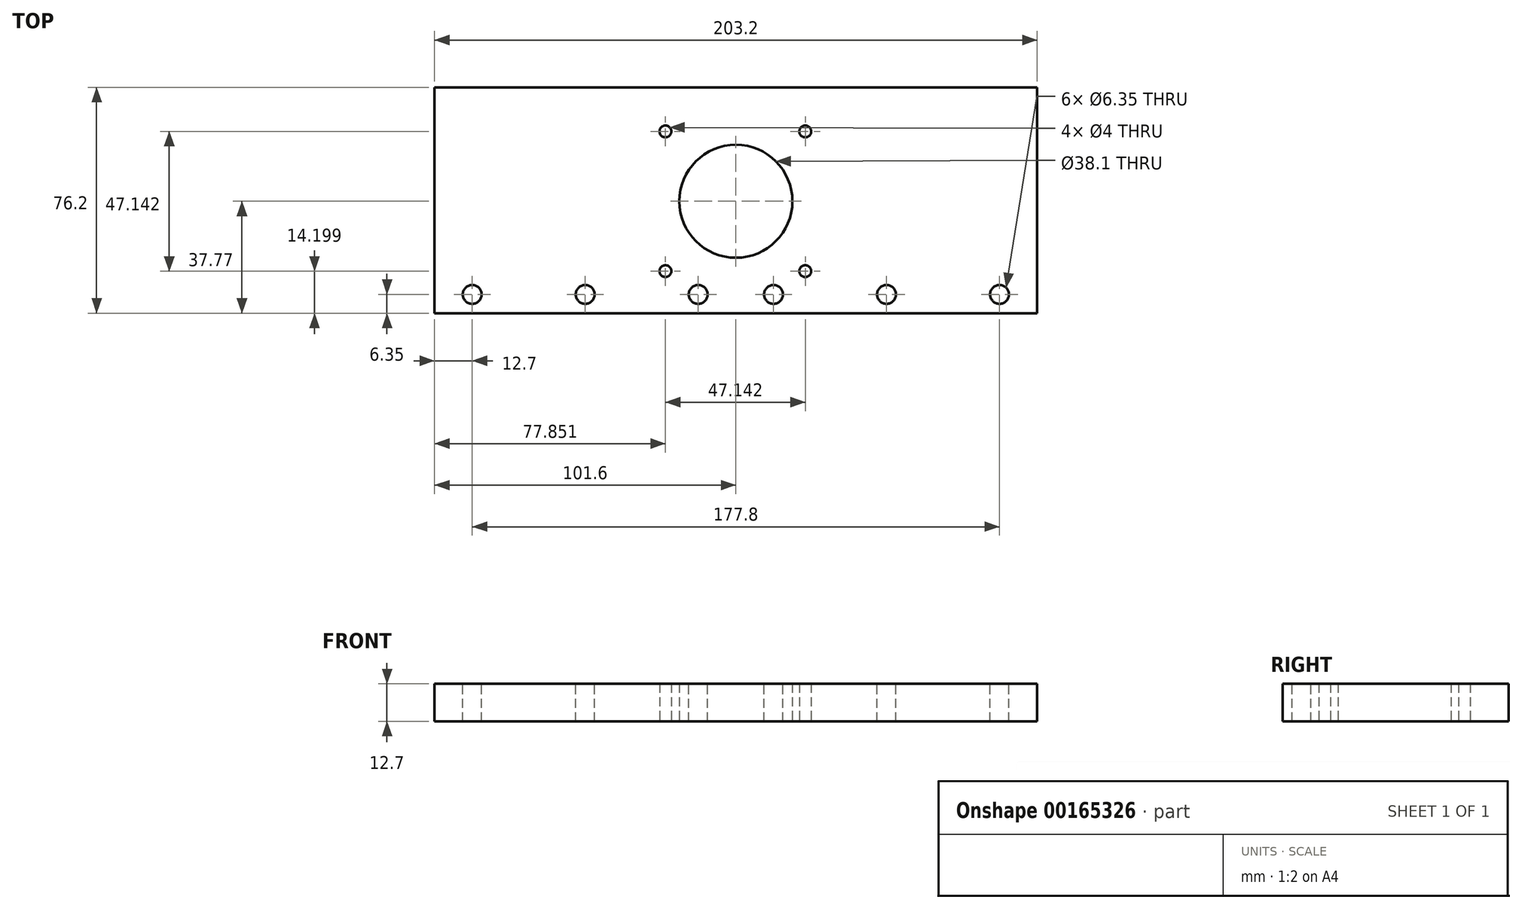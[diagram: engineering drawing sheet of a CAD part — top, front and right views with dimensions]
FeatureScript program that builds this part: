
annotation { "Feature Type Name" : "Feature", "Feature Type Description" : "" }
export const myFeature = defineFeature(function(context is Context, id is Id, definition is map)
    precondition{}
    {
        {
            var Q0;
            Q0=qCreatedBy(makeId("Top.planeOp"),FACE);
            var sketch = newSketch(context, id + "F0", { "sketchPlane" : qUnion([Q0])});
            skLineSegment(sketch, "E0.rect.bottom", {"start": v(101.6, -38.1) * mm, "end": v(-101.6, -38.1) * mm});
            skLineSegment(sketch, "E0.rect.top", {"start": v(101.6, 38.1) * mm, "end": v(-101.6, 38.1) * mm});
            skLineSegment(sketch, "E0.rect.left", {"start": v(101.6, -38.1) * mm, "end": v(101.6, 38.1) * mm});
            skLineSegment(sketch, "E0.rect.right", {"start": v(-101.6, -38.1) * mm, "end": v(-101.6, 38.1) * mm});
            skPoint(sketch, "E0.rect.middle", {"position": v(0, 0) * mm});
            skLineSegment(sketch, "E1", {"start": v(-101.6, 23.24) * mm, "end": v(101.6, 23.24) * mm, "construction": true});
            skLineSegment(sketch, "E2", {"start": v(101.6, 23.24) * mm, "end": v(102.39, 23.56) * mm, "construction": true});
            skLineSegment(sketch, "E3", {"start": v(-23.75, 38.1) * mm, "end": v(-23.75, -38.1) * mm, "construction": true});
            skLineSegment(sketch, "E4", {"start": v(-23.75, -38.1) * mm, "end": v(-24.87, -37.47) * mm, "construction": true});
            skLineSegment(sketch, "E5", {"start": v(-101.6, -23.9) * mm, "end": v(101.6, -23.9) * mm, "construction": true});
            skLineSegment(sketch, "E6", {"start": v(23.4, 38.1) * mm, "end": v(23.4, -38.1) * mm, "construction": true});
            skLineSegment(sketch, "E7", {"start": v(-23.75, 23.24) * mm, "end": v(23.4, -23.9) * mm, "construction": true});
            skLineSegment(sketch, "E8", {"start": v(23.4, 23.24) * mm, "end": v(-23.75, -23.9) * mm, "construction": true});
            skCircle(sketch, "E9", {"center": v(0, -0.33) * mm, "radius": 19.05 * mm});
            skPoint(sketch, "E9.centerSnap0", {"position": v(-0.18, -0.33) * mm});
            skCircle(sketch, "E10", {"center": v(-23.75, 23.24) * mm, "radius": 2 * mm});
            skCircle(sketch, "E11", {"center": v(-23.75, -23.9) * mm, "radius": 2 * mm});
            skCircle(sketch, "E12", {"center": v(23.4, -23.9) * mm, "radius": 2 * mm});
            skCircle(sketch, "E13", {"center": v(23.4, 23.24) * mm, "radius": 2 * mm});
            skSolve(sketch);
        }
        {
            var Q0;
            Q0=qSketchRegion(id+"F0",true);
            extrude(context, id + "F1", {"entities" : qUnion([Q0]), "depth" : 12.7 * mm});
        }
        {
            var Q0;
            Q0=makeQuery(id+"F1.opExtrude","CAP_FACE",FACE,{"disambiguationData":[OSD([sQuery(id+"F0.wireOp",EDGE,"E0.rect.bottom"),sQuery(id+"F0.wireOp",EDGE,"E0.rect.top"),sQuery(id+"F0.wireOp",EDGE,"E0.rect.left"),sQuery(id+"F0.wireOp",EDGE,"E0.rect.right"),sQuery(id+"F0.wireOp",EDGE,"E9"),sQuery(id+"F0.wireOp",EDGE,"E10"),sQuery(id+"F0.wireOp",EDGE,"E11"),sQuery(id+"F0.wireOp",EDGE,"E12"),sQuery(id+"F0.wireOp",EDGE,"E13")])],"isStart":false});
            var sketch = newSketch(context, id + "F2", { "sketchPlane" : qUnion([Q0])});
            skLineSegment(sketch, "E14", {"start": v(-101.6, -31.75) * mm, "end": v(101.6, -31.75) * mm, "construction": true});
            skLineSegment(sketch, "E15", {"start": v(-88.9, 38.1) * mm, "end": v(-88.9, -38.1) * mm, "construction": true});
            skLineSegment(sketch, "E16", {"start": v(-50.8, 38.1) * mm, "end": v(-50.8, -38.1) * mm, "construction": true});
            skLineSegment(sketch, "E17", {"start": v(-12.7, 38.1) * mm, "end": v(-12.7, -38.1) * mm, "construction": true});
            skLineSegment(sketch, "E18", {"start": v(12.7, 38.1) * mm, "end": v(12.7, -38.1) * mm, "construction": true});
            skLineSegment(sketch, "E19", {"start": v(50.8, 38.1) * mm, "end": v(50.8, -38.1) * mm, "construction": true});
            skLineSegment(sketch, "E20", {"start": v(88.9, 38.1) * mm, "end": v(88.9, -38.1) * mm, "construction": true});
            skCircle(sketch, "E21", {"center": v(-88.9, -31.75) * mm, "radius": 3.18 * mm});
            skCircle(sketch, "E22", {"center": v(-50.8, -31.75) * mm, "radius": 3.18 * mm});
            skCircle(sketch, "E23", {"center": v(-12.7, -31.75) * mm, "radius": 3.18 * mm});
            skCircle(sketch, "E24", {"center": v(12.7, -31.75) * mm, "radius": 3.18 * mm});
            skCircle(sketch, "E25", {"center": v(50.8, -31.75) * mm, "radius": 3.18 * mm});
            skCircle(sketch, "E26", {"center": v(88.9, -31.75) * mm, "radius": 3.18 * mm});
            skSolve(sketch);
        }
        {
            var Q0;
            Q0=qSketchRegion(id+"F2",true);
            extrude(context, id + "F3", {"entities" : qUnion([Q0]), "operationType" : NewBodyOperationType.REMOVE, "endBound" : BoundingType.THROUGH_ALL, "oppositeDirection" : true, "depth" : 25.4 * mm});
        }
    });
